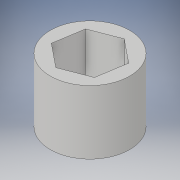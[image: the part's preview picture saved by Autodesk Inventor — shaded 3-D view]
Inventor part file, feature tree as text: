
AUTODESK INVENTOR PART (.ipt)
format: ipt  version: 2019 (Build 230136000, 136)  size: 98,816 bytes
history: native  units: in
note: dims shown in document units (in); Inventor stores cm internally (conversion verified against a paired STEP export)
features: extrude x1, sketch x1
ambient origin geometry x8: Origin, YZ Plane, XZ Plane, XY Plane, X Axis, Y Axis, Z Axis, Center Point
bodies: Solid1 (feature_tree)
feature tree (2):
  extrude  "Extrusion1"  Depth=0.625in TaperAngle=0.0deg
  sketch  "Sketch1"  dims[d0=0.29in d1=0.625in d2=0.0in]
